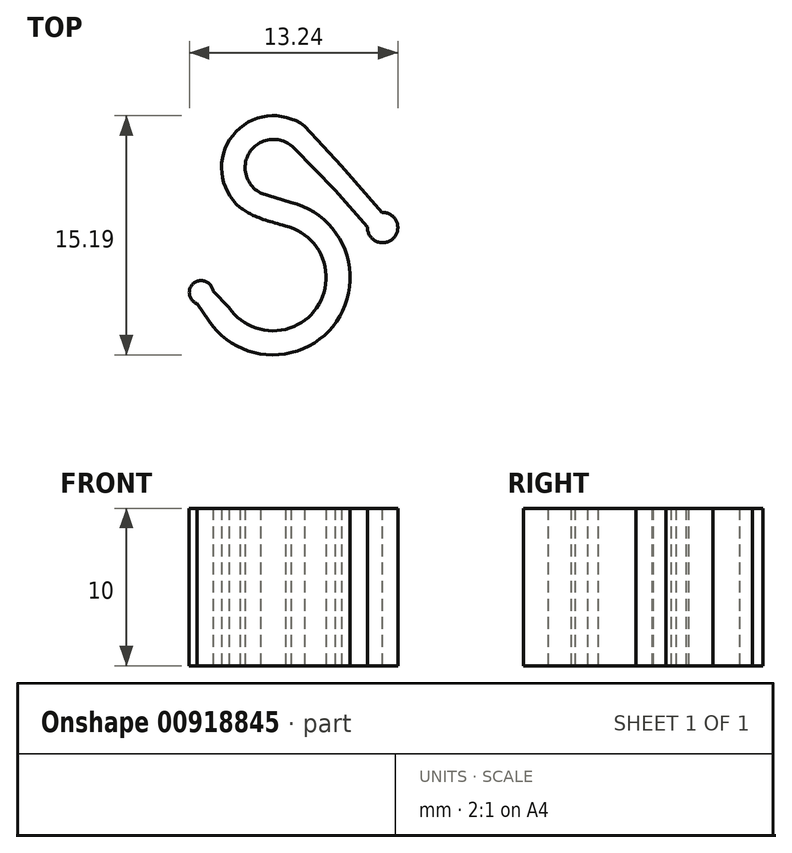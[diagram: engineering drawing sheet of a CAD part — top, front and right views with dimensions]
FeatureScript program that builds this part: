
annotation { "Feature Type Name" : "Feature", "Feature Type Description" : "" }
export const myFeature = defineFeature(function(context is Context, id is Id, definition is map)
    precondition{}
    {
        {
            var Q0;
            Q0=qCreatedBy(makeId("Top.planeOp"),FACE);
            var sketch = newSketch(context, id + "F0", { "sketchPlane" : qUnion([Q0])});
            skArc(sketch, "E0", {"start": v(-7.54, 8.93) * mm, "mid": v(-10.28, 8.75) * mm, "end": v(-9.66, 6.08) * mm});
            skLineSegment(sketch, "E1", {"start": v(-7.54, 8.93) * mm, "end": v(-4.94, 6.25) * mm});
            skArc(sketch, "E2.0", {"start": v(-6.85, 10.32) * mm, "mid": v(-11.42, 9.73) * mm, "end": v(-10.96, 5.15) * mm});
            skFitSpline(sketch, "E3", {"points": [v(-10.96, 5.15) * mm, v(-10.06, 4.63) * mm, v(-8.09, 3.99) * mm], "startDerivative": vector(1.9, -1.31) * mm, "endDerivative": vector(3.73, -1.04) * mm});
            skArc(sketch, "E4", {"start": v(-8.09, 3.99) * mm, "mid": v(-6.09, -1.22) * mm, "end": v(-11.66, -1.2) * mm});
            skArc(sketch, "E5.0", {"start": v(-7.73, 5.47) * mm, "mid": v(-4.83, -2.09) * mm, "end": v(-12.93, -2.07) * mm});
            skLineSegment(sketch, "E6", {"start": v(-9.66, 6.08) * mm, "end": v(-7.73, 5.47) * mm});
            skLineSegment(sketch, "E7", {"start": v(-6.85, 10.32) * mm, "end": v(-4.52, 7.8) * mm});
            skLineSegment(sketch, "E8", {"start": v(-4.94, 6.25) * mm, "end": v(-2.86, 3.92) * mm});
            skLineSegment(sketch, "E9", {"start": v(-4.52, 7.8) * mm, "end": v(-1.94, 4.84) * mm});
            skArc(sketch, "E10", {"start": v(-2.86, 3.92) * mm, "mid": v(-1.22, 3.2) * mm, "end": v(-1.94, 4.84) * mm});
            skLineSegment(sketch, "E11", {"start": v(-11.66, -1.2) * mm, "end": v(-12.67, -0.15) * mm});
            skLineSegment(sketch, "E12", {"start": v(-12.93, -2.07) * mm, "end": v(-13.68, -0.96) * mm});
            skArc(sketch, "E13", {"start": v(-12.67, -0.15) * mm, "mid": v(-13.9, 0.34) * mm, "end": v(-13.68, -0.96) * mm});
            skSolve(sketch);
        }
        {
            var Q0;
            Q0=makeQuery(id+"F0.imprint","IMPRINT",FACE,{"disambiguationData":[TD([[makeQuery(id+"F0.imprint","IMPRINT",EDGE,{"derivedFrom":sQuery(id+"F0.wireOp",EDGE,"E0")}),-1.0]])]});
            extrude(context, id + "F1", {"entities" : qUnion([Q0]), "depth" : 10 * mm, "offsetDistance" : 25 * mm});
        }
    });
